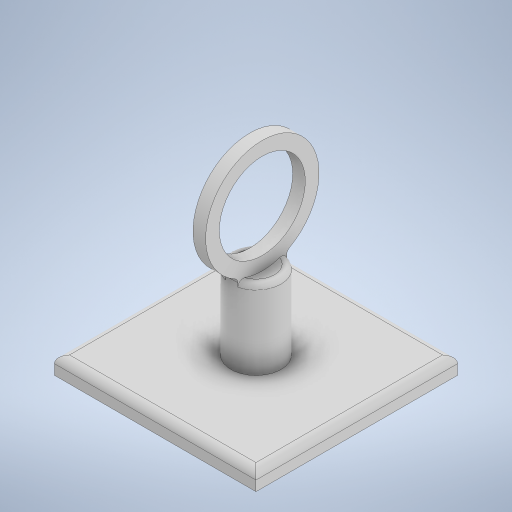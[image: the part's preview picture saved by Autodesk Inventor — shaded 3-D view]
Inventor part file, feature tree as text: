
AUTODESK INVENTOR PART (.ipt)
format: ipt  version: 2024.2 (Build 282272000, 272)  size: 311,296 bytes
history: native  units: in
note: dims shown in document units (in); Inventor stores cm internally (conversion verified against a paired STEP export)
features: sketch x3, extrude x2, fillet x2, plane x1, revolve x1
ambient origin geometry x8: Origin, YZ Plane, XZ Plane, XY Plane, X Axis, Y Axis, Z Axis, Center Point
bodies: Solid1 (feature_tree)
feature tree (9):
  extrude  "Extrusion1"  Depth=1.7717in
  plane  "Work Plane1"
  revolve  "Revolution1"  [1 undecoded]
  fillet  "Fillet1"  Radius=0.3937in
  extrude  "Extrusion2"  Depth=0.1181in
  fillet  "Fillet2"  Radius=1.5748in
  sketch  "Sketch1"  dims[d0=1.3441in d1=1.7717in]
  sketch  "Sketch4"  dims[d2=0.1969in d3=0.0in d11=1.1811in d12=0.3937in]
  sketch  "Sketch5"  dims[d13=90.0deg d14=0.0787in d18=1.5748in d19=3.1496in d20=3.1496in d21=3.1496in d22=0.2756in d23=0.0in d24=0.1181in d9=0.0344in d10=0.0344in]
note: 1 required parameter value undecoded (feature->parameter linkage not recoverable at this tier; creation-order binding heuristic only, values carry confidence <= 0.55)
